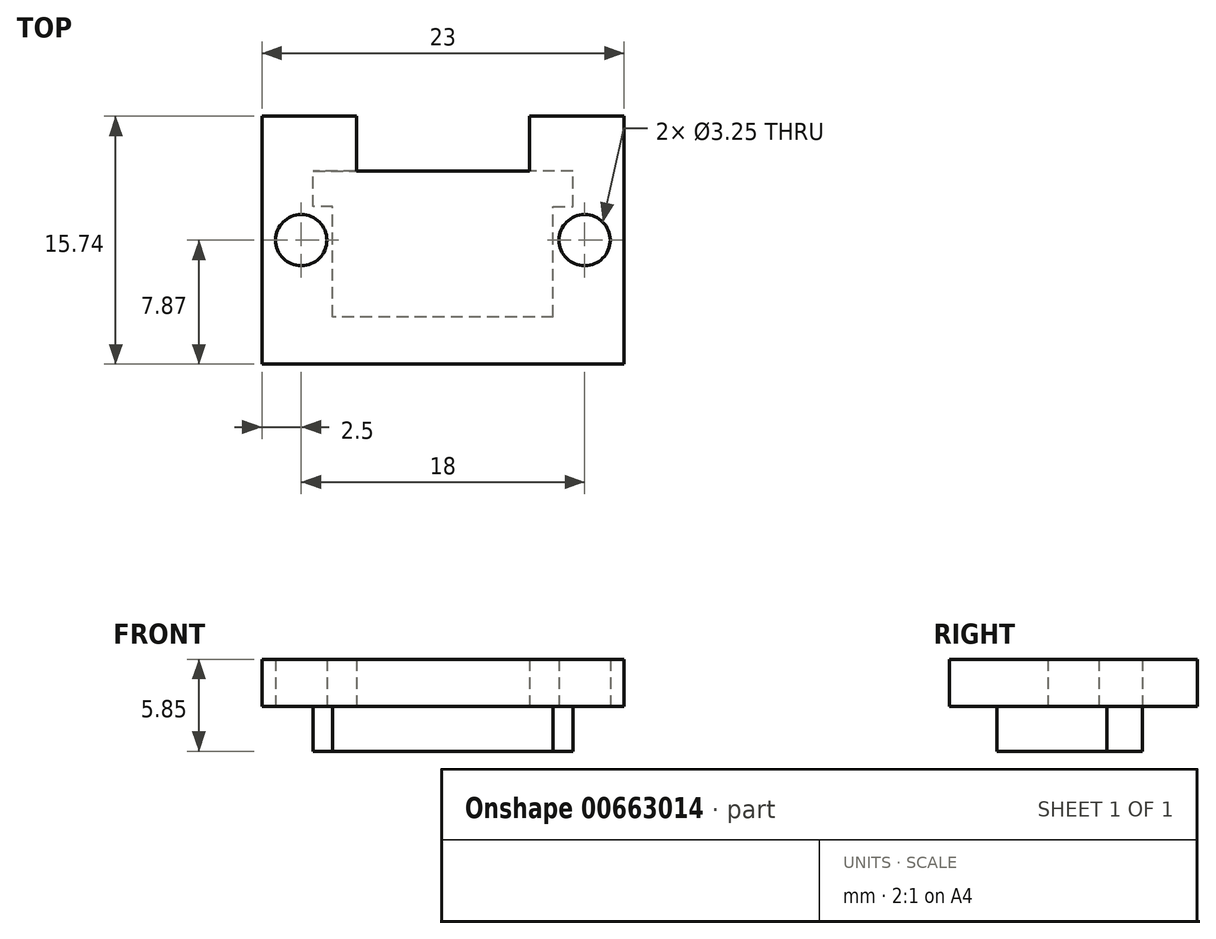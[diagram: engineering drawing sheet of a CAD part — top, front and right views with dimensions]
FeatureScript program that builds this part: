
annotation { "Feature Type Name" : "Feature", "Feature Type Description" : "" }
export const myFeature = defineFeature(function(context is Context, id is Id, definition is map)
    precondition{}
    {
        {
            var Q0;
            Q0=qCreatedBy(makeId("Top.planeOp"),FACE);
            var sketch = newSketch(context, id + "F0", { "sketchPlane" : qUnion([Q0])});
            skLineSegment(sketch, "E0.bottom", {"start": v(11.5, -4.62) * mm, "end": v(-11.5, -4.63) * mm});
            skLineSegment(sketch, "E0.top", {"start": v(11.5, 4.63) * mm, "end": v(-11.5, 4.62) * mm});
            skLineSegment(sketch, "E0.left", {"start": v(11.5, -4.62) * mm, "end": v(11.5, 4.63) * mm});
            skLineSegment(sketch, "E0.right", {"start": v(-11.5, -4.63) * mm, "end": v(-11.5, 4.62) * mm});
            skPoint(sketch, "E0.middle", {"position": v(0, 0) * mm});
            skSolve(sketch);
        }
        {
            var Q0;
            Q0=makeQuery(id+"F0.imprint","IMPRINT",FACE,{"disambiguationData":[TD([[makeQuery(id+"F0.imprint","IMPRINT",EDGE,{"derivedFrom":sQuery(id+"F0.wireOp",EDGE,"E0.bottom")}),-1.0]])]});
            extrude(context, id + "F1", {"entities" : qUnion([Q0]), "depth" : 3 * mm, "offsetDistance" : 25 * mm});
        }
        {
            var Q0;
            Q0=makeQuery(id+"F1.opExtrude","CAP_FACE",FACE,{"disambiguationData":[OSD([sQuery(id+"F0.wireOp",EDGE,"E0.bottom"),sQuery(id+"F0.wireOp",EDGE,"E0.top"),sQuery(id+"F0.wireOp",EDGE,"E0.left"),sQuery(id+"F0.wireOp",EDGE,"E0.right")])],"isStart":true});
            var sketch = newSketch(context, id + "F2", { "sketchPlane" : qUnion([Q0])});
            skLineSegment(sketch, "E1", {"start": v(-7, 4.63) * mm, "end": v(-7, 1.13) * mm});
            skLineSegment(sketch, "E2", {"start": v(-7, 1.13) * mm, "end": v(-8.25, 1.13) * mm});
            skLineSegment(sketch, "E3", {"start": v(-8.25, 1.13) * mm, "end": v(-8.25, -1.13) * mm});
            skLineSegment(sketch, "E4", {"start": v(-8.25, -1.13) * mm, "end": v(-5.5, -1.13) * mm});
            skLineSegment(sketch, "E5", {"start": v(-5.5, -1.13) * mm, "end": v(-5.5, -4.62) * mm});
            skLineSegment(sketch, "E6", {"start": v(7, 4.62) * mm, "end": v(7, 1.13) * mm});
            skLineSegment(sketch, "E7", {"start": v(7, 1.13) * mm, "end": v(8.25, 1.13) * mm});
            skLineSegment(sketch, "E8", {"start": v(8.25, 1.13) * mm, "end": v(8.25, -1.12) * mm});
            skLineSegment(sketch, "E9", {"start": v(8.25, -1.12) * mm, "end": v(5.5, -1.12) * mm});
            skLineSegment(sketch, "E10", {"start": v(5.5, -1.12) * mm, "end": v(5.5, -4.63) * mm});
            skSolve(sketch);
        }
        {
            var Q0;
            {var subQ3=sQuery(id+"F2.wireOp",EDGE,"E1");Q0=makeQuery(id+"F2.imprint","IMPRINT",FACE,{"disambiguationData":[TD([[makeQuery(id+"F2.imprint","IMPRINT",EDGE,{"derivedFrom":subQ3}),1.0]])]});}
            extrude(context, id + "F3", {"entities" : qUnion([Q0]), "operationType" : NewBodyOperationType.ADD, "depth" : 3.6 * mm, "offsetDistance" : 25 * mm});
        }
        {
            var Q0;
            Q0=makeQuery(id+"F3.opExtrude","CAP_FACE",FACE,{"disambiguationData":[OSD([sQuery(id+"F0.wireOp",EDGE,"E0.bottom"),sQuery(id+"F0.wireOp",EDGE,"E0.top"),sQuery(id+"F2.wireOp",EDGE,"E1"),sQuery(id+"F2.wireOp",EDGE,"E2"),sQuery(id+"F2.wireOp",EDGE,"E3"),sQuery(id+"F2.wireOp",EDGE,"E4"),sQuery(id+"F2.wireOp",EDGE,"E5"),sQuery(id+"F2.wireOp",EDGE,"E6"),sQuery(id+"F2.wireOp",EDGE,"E7"),sQuery(id+"F2.wireOp",EDGE,"E8"),sQuery(id+"F2.wireOp",EDGE,"E9"),sQuery(id+"F2.wireOp",EDGE,"E10")])],"isStart":false});
            var sketch = newSketch(context, id + "F4", { "sketchPlane" : qUnion([Q0])});
            skLineSegment(sketch, "E11.bottom", {"start": v(5.5, -4.63) * mm, "end": v(-5.5, -4.63) * mm});
            skLineSegment(sketch, "E11.top", {"start": v(5.5, -1.13) * mm, "end": v(-5.5, -1.13) * mm});
            skLineSegment(sketch, "E11.left", {"start": v(5.5, -4.63) * mm, "end": v(5.5, -1.13) * mm});
            skLineSegment(sketch, "E11.right", {"start": v(-5.5, -4.63) * mm, "end": v(-5.5, -1.13) * mm});
            skSolve(sketch);
        }
        {
            var Q0;
            Q0=makeQuery(id+"F4.imprint","IMPRINT",FACE,{"disambiguationData":[TD([[makeQuery(id+"F4.imprint","IMPRINT",EDGE,{"derivedFrom":sQuery(id+"F4.wireOp",EDGE,"E11.bottom")}),-1.0]])]});
            extrude(context, id + "F5", {"entities" : qUnion([Q0]), "operationType" : NewBodyOperationType.REMOVE, "endBound" : BoundingType.THROUGH_ALL, "oppositeDirection" : true, "depth" : 3 * mm, "offsetDistance" : 25 * mm});
        }
        {
            var Q0;
            Q0=makeQuery(id+"F3.opExtrude","CAP_FACE",FACE,{"disambiguationData":[OSD([sQuery(id+"F0.wireOp",EDGE,"E0.bottom"),sQuery(id+"F0.wireOp",EDGE,"E0.top"),sQuery(id+"F2.wireOp",EDGE,"E1"),sQuery(id+"F2.wireOp",EDGE,"E2"),sQuery(id+"F2.wireOp",EDGE,"E3"),sQuery(id+"F2.wireOp",EDGE,"E4"),sQuery(id+"F2.wireOp",EDGE,"E5"),sQuery(id+"F2.wireOp",EDGE,"E6"),sQuery(id+"F2.wireOp",EDGE,"E7"),sQuery(id+"F2.wireOp",EDGE,"E8"),sQuery(id+"F2.wireOp",EDGE,"E9"),sQuery(id+"F2.wireOp",EDGE,"E10")])],"isStart":false});
            var sketch = newSketch(context, id + "F6", { "sketchPlane" : qUnion([Q0])});
            skLineSegment(sketch, "E12.bottom", {"start": v(8.25, -1.12) * mm, "end": v(-8.25, -1.12) * mm});
            skLineSegment(sketch, "E12.top", {"start": v(8.25, 1.13) * mm, "end": v(-8.25, 1.13) * mm});
            skLineSegment(sketch, "E12.left", {"start": v(8.25, -1.12) * mm, "end": v(8.25, 1.13) * mm});
            skLineSegment(sketch, "E12.right", {"start": v(-8.25, -1.12) * mm, "end": v(-8.25, 1.13) * mm});
            skSolve(sketch);
        }
        {
            var Q0;
            Q0=makeQuery(id+"F6.imprint","IMPRINT",FACE,{"disambiguationData":[TD([[makeQuery(id+"F6.imprint","IMPRINT",EDGE,{"derivedFrom":sQuery(id+"F6.wireOp",EDGE,"E12.bottom")}),-1.0]])]});
            extrude(context, id + "F7", {"entities" : qUnion([Q0]), "operationType" : NewBodyOperationType.REMOVE, "oppositeDirection" : true, "depth" : 0.75 * mm, "offsetDistance" : 25 * mm});
        }
        {
            var Q0;
            Q0=makeQuery(id+"F7.boolean.opBoolean","COPY",FACE,{"derivedFrom":makeQuery(id+"F7.opExtrude","SWEPT_FACE",FACE,{"disambiguationData":[OSD([sQuery(id+"F6.wireOp",EDGE,"E12.top")])]})});
            extrude(context, id + "F8", {"entities" : qUnion([Q0]), "operationType" : NewBodyOperationType.REMOVE, "endBound" : BoundingType.THROUGH_ALL, "oppositeDirection" : true, "depth" : 25 * mm, "offsetDistance" : 25 * mm});
        }
        {
            var Q0;
            {var subQ0=sQuery(id+"F0.wireOp",EDGE,"E0.bottom");Q0=makeQuery(id+"F3.boolean.opBoolean","MERGE",FACE,{"derivedFrom":[makeQuery(id+"F1.opExtrude","SWEPT_FACE",FACE,{"disambiguationData":[OSD([subQ0])]}),makeQuery(id+"F3.opExtrude","SWEPT_FACE",FACE,{"disambiguationData":[OSD([subQ0])]})]});}
            extrude(context, id + "F9", {"entities" : qUnion([Q0]), "operationType" : NewBodyOperationType.ADD, "depth" : 3.5 * mm, "offsetDistance" : 25 * mm});
        }
        {
            var Q0;
            Q0=makeQuery(id+"F9.opExtrude","CAP_FACE",FACE,{"disambiguationData":[OSD([sQuery(id+"F0.wireOp",EDGE,"E0.bottom")])],"isStart":false});
            var sketch = newSketch(context, id + "F10", { "sketchPlane" : qUnion([Q0])});
            skLineSegment(sketch, "E13.bottom", {"start": v(-11.5, 3) * mm, "end": v(11.5, 3) * mm});
            skLineSegment(sketch, "E13.top", {"start": v(-11.5, 0) * mm, "end": v(11.5, 0) * mm});
            skLineSegment(sketch, "E13.left", {"start": v(-11.5, 3) * mm, "end": v(-11.5, 0) * mm});
            skLineSegment(sketch, "E13.right", {"start": v(11.5, 3) * mm, "end": v(11.5, 0) * mm});
            skSolve(sketch);
        }
        {
            var Q0;
            Q0=makeQuery(id+"F10.imprint","IMPRINT",FACE,{"disambiguationData":[TD([[makeQuery(id+"F10.imprint","IMPRINT",EDGE,{"derivedFrom":sQuery(id+"F10.wireOp",EDGE,"E13.bottom")}),1.0]])]});
            extrude(context, id + "F11", {"entities" : qUnion([Q0]), "operationType" : NewBodyOperationType.ADD, "depth" : 3 * mm, "offsetDistance" : 25 * mm});
        }
        {
            var Q0;
            {var subQ0=sQuery(id+"F0.wireOp",EDGE,"E0.right");var subQ1=sQuery(id+"F0.wireOp",EDGE,"E0.left");var subQ2=sQuery(id+"F0.wireOp",EDGE,"E0.top");var subQ3=sQuery(id+"F0.wireOp",EDGE,"E0.bottom");var subQ4=makeQuery(id+"F1.opExtrude","CAP_FACE",FACE,{"disambiguationData":[OSD([subQ3,subQ2,subQ1,subQ0])],"isStart":true});var subQ6=makeQuery(id+"F1.opExtrude","SWEPT_FACE",FACE,{"disambiguationData":[OSD([subQ0])]});var subQ9=makeQuery(id+"F1.opExtrude","CAP_EDGE",EDGE,{"disambiguationData":[OSD([subQ3])],"isStart":true});var subQ13=makeQuery(id+"F1.opExtrude","SWEPT_FACE",FACE,{"disambiguationData":[OSD([subQ1])]});Q0=makeQuery(id+"F11.boolean.opBoolean","MERGE",FACE,{"derivedFrom":[makeQuery(id+"F9.boolean.opBoolean","MERGE",FACE,{"derivedFrom":[makeQuery(id+"F3.boolean.opBoolean","SPLIT",FACE,{"disambiguationData":[TD([subQ13])],"derivedFrom":subQ4}),makeQuery(id+"F9.opExtrude","SWEPT_FACE",FACE,{"disambiguationData":[OSD([subQ3]),TDD([makeQuery(id+"F3.boolean.opBoolean","SPLIT",EDGE,{"disambiguationData":[TD([subQ13])],"derivedFrom":subQ9})])]})]}),makeQuery(id+"F9.boolean.opBoolean","MERGE",FACE,{"derivedFrom":[makeQuery(id+"F3.boolean.opBoolean","SPLIT",FACE,{"disambiguationData":[TD([subQ6])],"derivedFrom":subQ4}),makeQuery(id+"F9.opExtrude","SWEPT_FACE",FACE,{"disambiguationData":[OSD([subQ3]),TDD([makeQuery(id+"F3.boolean.opBoolean","SPLIT",EDGE,{"disambiguationData":[TD([subQ6])],"derivedFrom":subQ9})])]})]}),makeQuery(id+"F11.opExtrude","SWEPT_FACE",FACE,{"disambiguationData":[OSD([sQuery(id+"F10.wireOp",EDGE,"E13.top")])]})]});}
            var sketch = newSketch(context, id + "F12", { "sketchPlane" : qUnion([Q0])});
            skCircle(sketch, "E14", {"center": v(-9, 3.25) * mm, "radius": 1.63 * mm});
            skCircle(sketch, "E15", {"center": v(9, 3.25) * mm, "radius": 1.63 * mm});
            skSolve(sketch);
        }
        {
            var Q0;
            Q0=makeQuery(id+"F12.imprint","IMPRINT",FACE,{"disambiguationData":[TD([[makeQuery(id+"F12.imprint","IMPRINT",EDGE,{"derivedFrom":sQuery(id+"F12.wireOp",EDGE,"E14")}),1.0]])]});
            var Q1;
            Q1=makeQuery(id+"F12.imprint","IMPRINT",FACE,{"disambiguationData":[TD([[makeQuery(id+"F12.imprint","IMPRINT",EDGE,{"derivedFrom":sQuery(id+"F12.wireOp",EDGE,"E15")}),1.0]])]});
            extrude(context, id + "F13", {"entities" : qUnion([Q0, Q1]), "operationType" : NewBodyOperationType.REMOVE, "endBound" : BoundingType.THROUGH_ALL, "oppositeDirection" : true, "depth" : 25 * mm, "offsetDistance" : 25 * mm});
        }
    });
